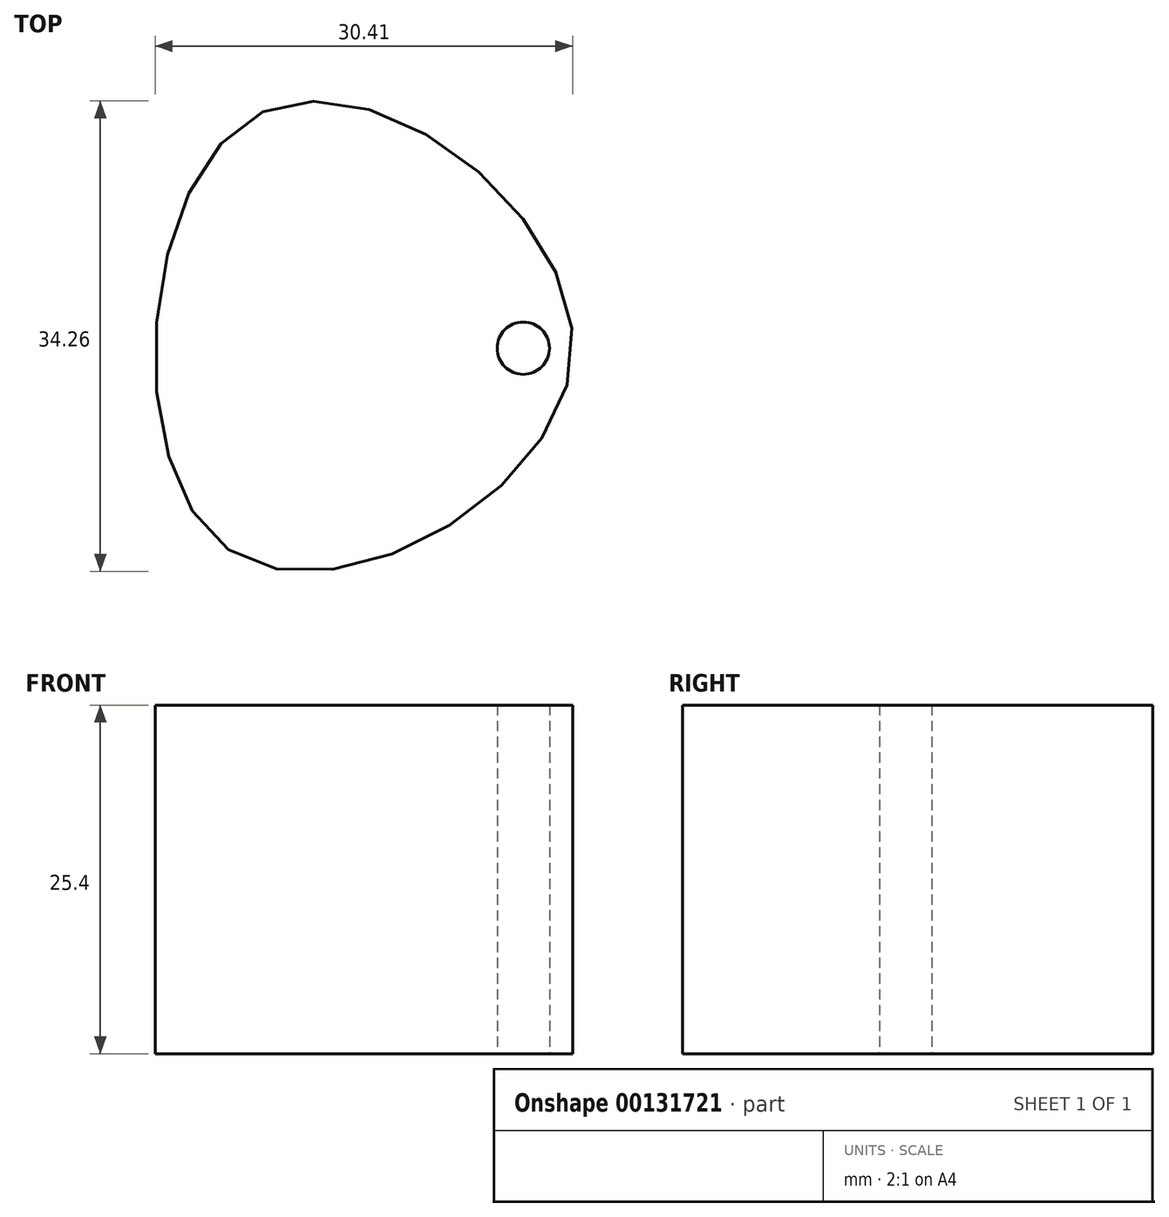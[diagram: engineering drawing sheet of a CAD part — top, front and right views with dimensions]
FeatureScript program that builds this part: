
annotation { "Feature Type Name" : "Feature", "Feature Type Description" : "" }
export const myFeature = defineFeature(function(context is Context, id is Id, definition is map)
    precondition{}
    {
        {
            var Q0;
            Q0=qCreatedBy(makeId("Top.planeOp"),FACE);
            var sketch = newSketch(context, id + "F0", { "sketchPlane" : qUnion([Q0])});
            skFitSpline(sketch, "E0", {"points": [v(-23.68, -14.2) * mm, v(-21.42, 17.6) * mm, v(1.36, 0) * mm, v(-23.68, -14.2) * mm]});
            skSolve(sketch);
        }
        {
            var Q0;
            Q0=makeQuery(id+"F0.imprint","IMPRINT",FACE,{"disambiguationData":[TD([[makeQuery(id+"F0.imprint","IMPRINT",EDGE,{"derivedFrom":sQuery(id+"F0.wireOp",EDGE,"E0")}),-1.0]])]});
            extrude(context, id + "F1", {"entities" : qUnion([Q0]), "oppositeDirection" : true, "depth" : 25.4 * mm});
        }
        {
            var Q0;
            Q0=makeQuery(id+"F1.opExtrude","CAP_FACE",FACE,{"disambiguationData":[OSD([sQuery(id+"F0.wireOp",EDGE,"E0")])],"isStart":false});
            var sketch = newSketch(context, id + "F2", { "sketchPlane" : qUnion([Q0])});
            skCircle(sketch, "E1", {"center": v(-2.2, -0.48) * mm, "radius": 1.9 * mm});
            skSolve(sketch);
        }
        {
            var Q0;
            Q0 = qSketchRegion(id + "F2", true);
            extrude(context, id + "F3", {"entities" : qUnion([Q0]), "operationType" : NewBodyOperationType.REMOVE, "oppositeDirection" : true, "depth" : 25.4 * mm});
        }
    });
